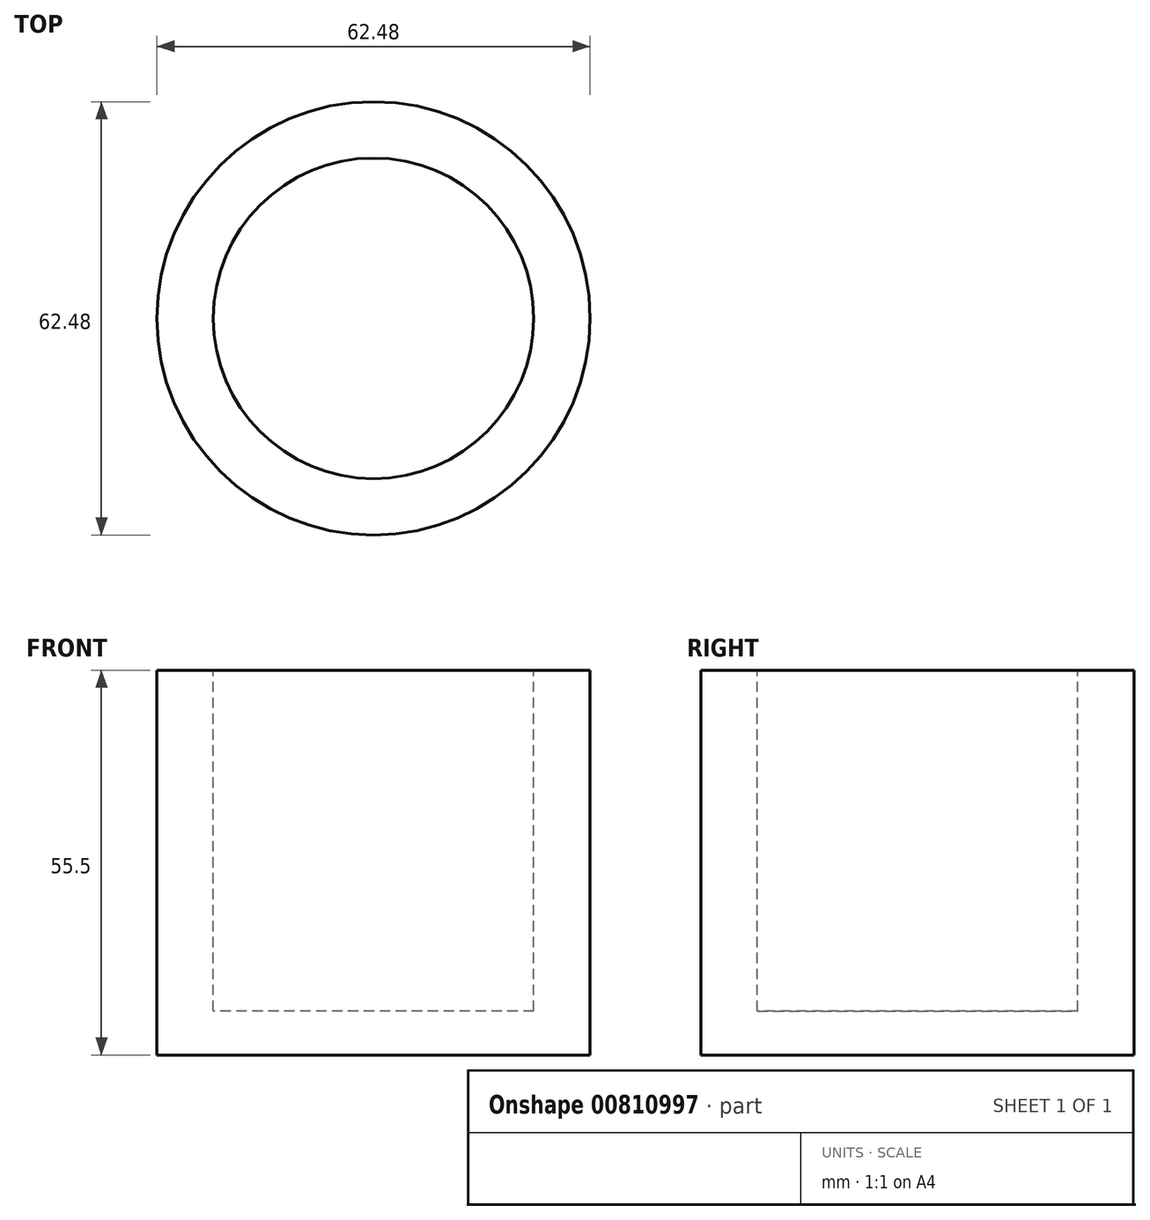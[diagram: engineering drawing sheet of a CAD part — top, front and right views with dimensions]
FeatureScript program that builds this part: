
annotation { "Feature Type Name" : "Feature", "Feature Type Description" : "" }
export const myFeature = defineFeature(function(context is Context, id is Id, definition is map)
    precondition{}
    {
        {
            var Q0;
            Q0=qCreatedBy(makeId("Front.planeOp"),FACE);
            var sketch = newSketch(context, id + "F0", { "sketchPlane" : qUnion([Q0])});
            skLineSegment(sketch, "E0", {"start": v(0, 0) * mm, "end": v(0, 49.03) * mm, "construction": true});
            skLineSegment(sketch, "E1", {"start": v(0, 0) * mm, "end": v(31.24, 0) * mm});
            skLineSegment(sketch, "E2", {"start": v(31.24, 0) * mm, "end": v(31.24, 55.5) * mm});
            skLineSegment(sketch, "E3", {"start": v(31.24, 55.5) * mm, "end": v(23.11, 55.5) * mm});
            skLineSegment(sketch, "E4", {"start": v(23.11, 55.5) * mm, "end": v(23.11, 6.35) * mm});
            skLineSegment(sketch, "E5", {"start": v(23.11, 6.35) * mm, "end": v(0, 6.35) * mm});
            skLineSegment(sketch, "E6.MirrorCS", {"start": v(-23.11, 55.5) * mm, "end": v(-23.11, 6.35) * mm});
            skLineSegment(sketch, "E7.MirrorCS", {"start": v(-31.24, 55.5) * mm, "end": v(-23.11, 55.5) * mm});
            skLineSegment(sketch, "E8.MirrorCS", {"start": v(-31.24, 0) * mm, "end": v(-31.24, 55.5) * mm});
            skLineSegment(sketch, "E9.MirrorCS", {"start": v(-23.11, 6.35) * mm, "end": v(0, 6.35) * mm});
            skLineSegment(sketch, "E10.MirrorCS", {"start": v(0, 0) * mm, "end": v(-31.24, 0) * mm});
            skLineSegment(sketch, "E11", {"start": v(0, 6.35) * mm, "end": v(0, 0) * mm});
            skSolve(sketch);
        }
        {
            var Q0;
            Q0=makeQuery(id+"F0.imprint","IMPRINT",FACE,{"disambiguationData":[TD([[makeQuery(id+"F0.imprint","IMPRINT",EDGE,{"derivedFrom":sQuery(id+"F0.wireOp",EDGE,"E1")}),1.0]])]});
            var Q1;
            Q1=sQuery(id+"F0.wireOp",EDGE,"E11");
            revolve(context, id + "F1", {"surfaceOperationType" : NewSurfaceOperationType.NEW, "entities" : qUnion([Q0]), "axis" : qUnion([Q1]), "revolveType" : RevolveType.FULL});
        }
    });
